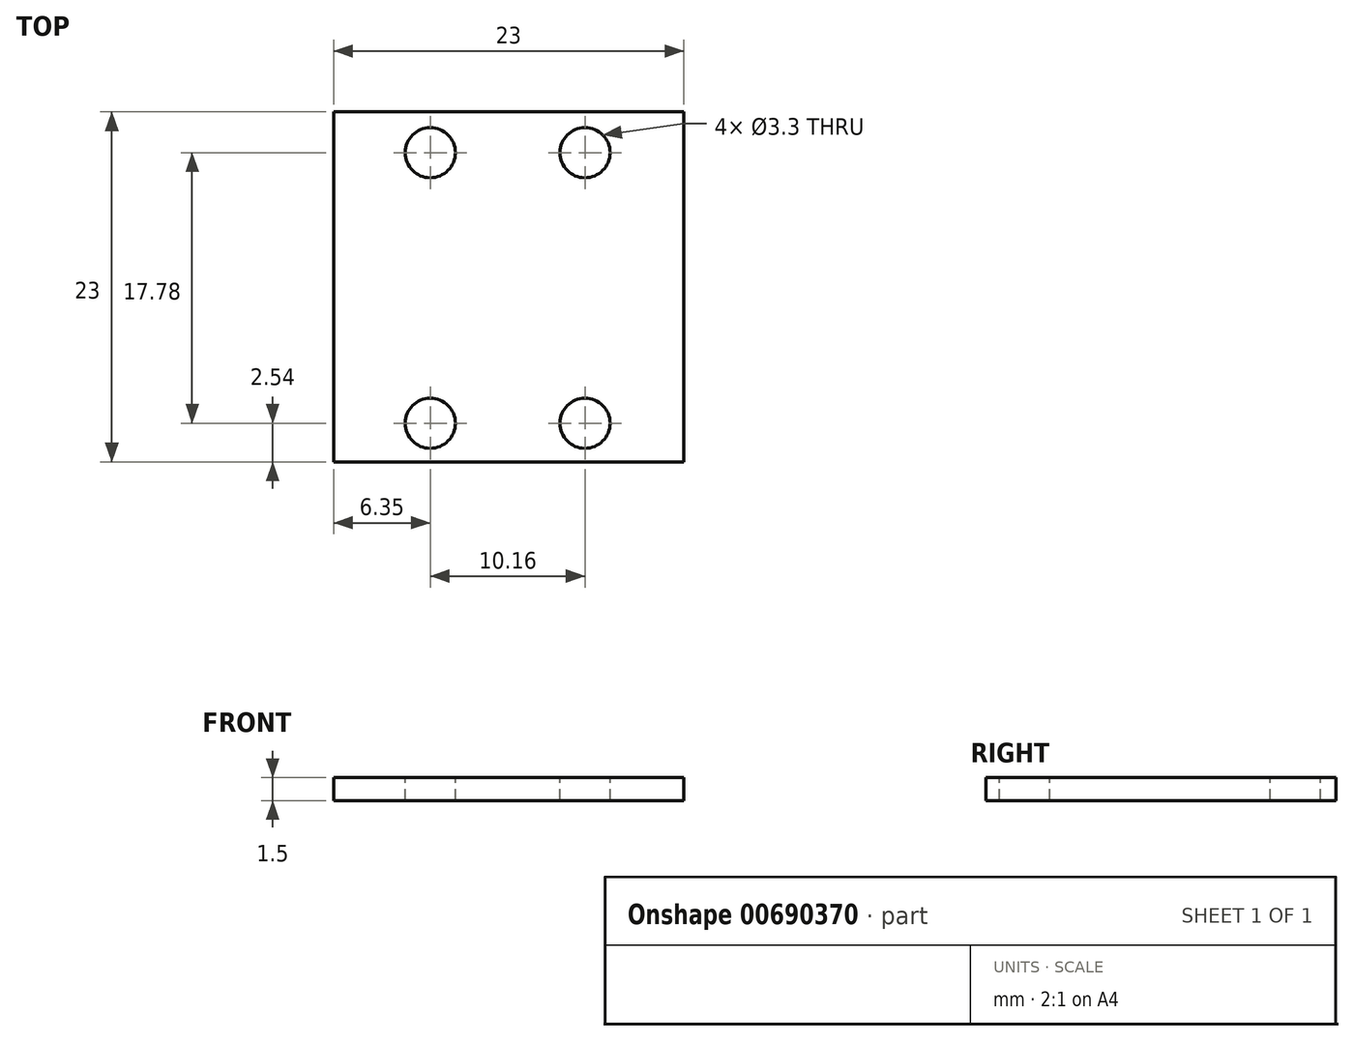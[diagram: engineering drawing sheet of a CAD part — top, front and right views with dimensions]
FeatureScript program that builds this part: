
annotation { "Feature Type Name" : "Feature", "Feature Type Description" : "" }
export const myFeature = defineFeature(function(context is Context, id is Id, definition is map)
    precondition{}
    {
        {
            var Q0;
            Q0=qCreatedBy(makeId("Top.planeOp"),FACE);
            var sketch = newSketch(context, id + "F0", { "sketchPlane" : qUnion([Q0])});
            skLineSegment(sketch, "E0.bottom", {"start": v(-11.5, 11.5) * mm, "end": v(11.5, 11.5) * mm});
            skLineSegment(sketch, "E0.top", {"start": v(-11.5, -11.5) * mm, "end": v(11.5, -11.5) * mm});
            skLineSegment(sketch, "E0.left", {"start": v(-11.5, 11.5) * mm, "end": v(-11.5, -11.5) * mm});
            skLineSegment(sketch, "E0.right", {"start": v(11.5, 11.5) * mm, "end": v(11.5, -11.5) * mm});
            skPoint(sketch, "E0.middle", {"position": v(0, 0) * mm});
            skSolve(sketch);
        }
        {
            var Q0;
            Q0 = qSketchRegion(id + "F0", true);
            extrude(context, id + "F1", {"entities" : qUnion([Q0]), "depth" : 1.5 * mm, "offsetDistance" : 25.4 * mm});
        }
        {
            var Q0;
            Q0=makeQuery(id+"F1.opExtrude","CAP_FACE",FACE,{"disambiguationData":[OSD([sQuery(id+"F0.wireOp",EDGE,"E0.bottom"),sQuery(id+"F0.wireOp",EDGE,"E0.top"),sQuery(id+"F0.wireOp",EDGE,"E0.left"),sQuery(id+"F0.wireOp",EDGE,"E0.right")])],"isStart":false});
            var sketch = newSketch(context, id + "F2", { "sketchPlane" : qUnion([Q0])});
            skCircle(sketch, "E1", {"center": v(-5.15, -8.96) * mm, "radius": 1.65 * mm});
            skCircle(sketch, "E2", {"center": v(5, -8.96) * mm, "radius": 1.65 * mm});
            skCircle(sketch, "E3", {"center": v(-5.15, 8.82) * mm, "radius": 1.65 * mm});
            skCircle(sketch, "E4", {"center": v(5, 8.82) * mm, "radius": 1.65 * mm});
            skSolve(sketch);
        }
        {
            var Q0;
            Q0 = qSketchRegion(id + "F2", true);
            extrude(context, id + "F3", {"entities" : qUnion([Q0]), "operationType" : NewBodyOperationType.REMOVE, "endBound" : BoundingType.THROUGH_ALL, "oppositeDirection" : true, "depth" : 25.4 * mm, "offsetDistance" : 25.4 * mm});
        }
    });
